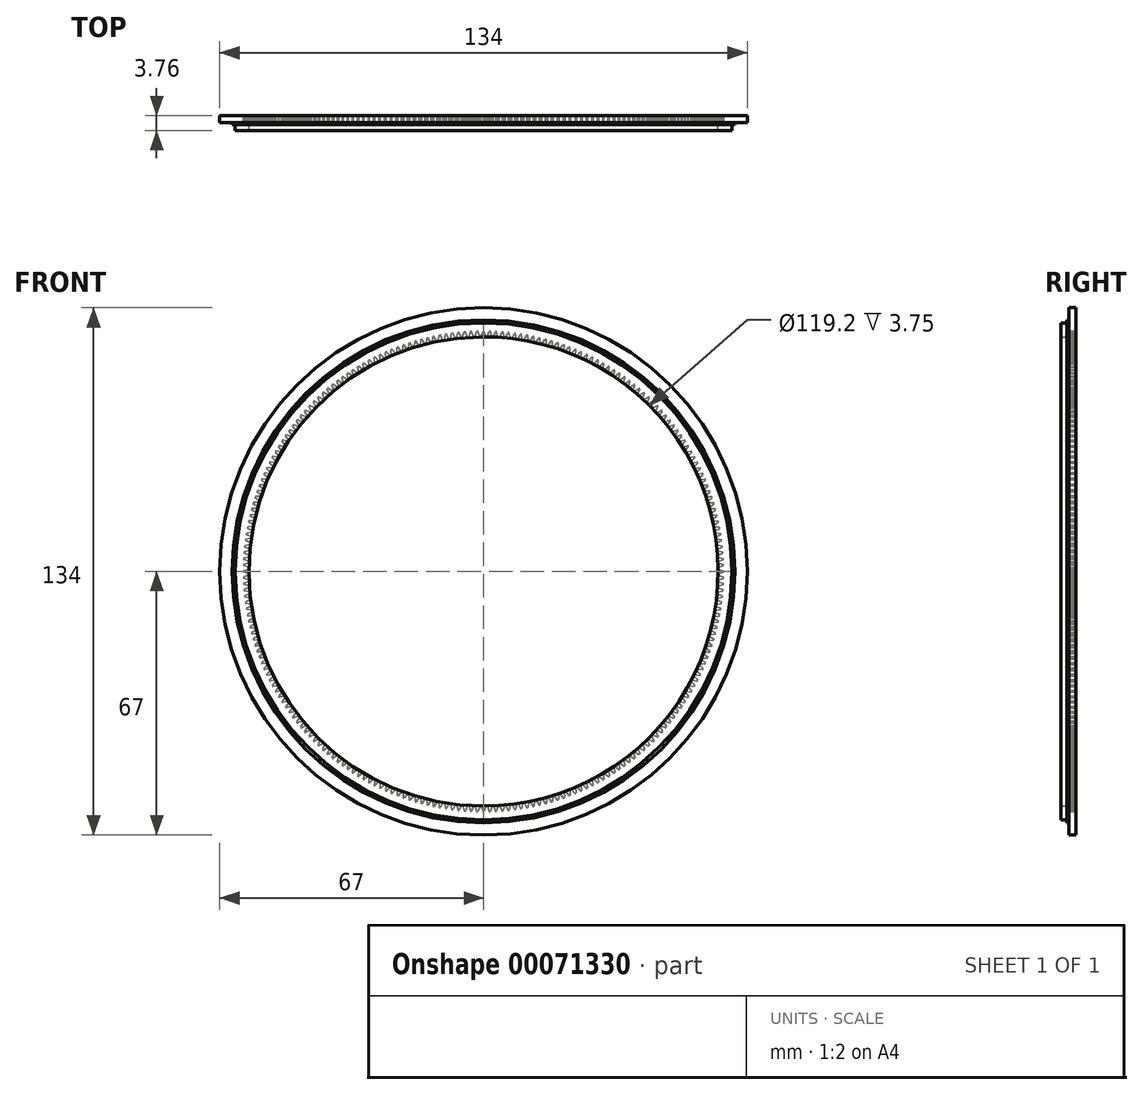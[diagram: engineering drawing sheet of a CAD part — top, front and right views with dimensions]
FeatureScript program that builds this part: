
annotation { "Feature Type Name" : "Feature", "Feature Type Description" : "" }
export const myFeature = defineFeature(function(context is Context, id is Id, definition is map)
    precondition{}
    {
        {
            var Q0;
            Q0=qCreatedBy(makeId("Front.planeOp"),FACE);
            var sketch = newSketch(context, id + "F0", { "sketchPlane" : qUnion([Q0])});
            skCircle(sketch, "E0", {"center": v(0, 0) * mm, "radius": 59.6 * mm});
            skCircle(sketch, "E1", {"center": v(0, 0) * mm, "radius": 67 * mm});
            skSolve(sketch);
        }
        {
            var Q0;
            Q0 = qSketchRegion(id + "F0", true);
            var Q1;
            Q1 = qSketchRegion(id + "F2", true);
            extrude(context, id + "F1", {"entities" : qUnion([Q0, Q1]), "endBound" : BoundingType.SYMMETRIC, "depth" : 3.75 * mm});
        }
        {
            var Q0;
            Q0=makeQuery(id+"F1.opExtrude","CAP_FACE",FACE,{"disambiguationData":[OSD([sQuery(id+"F0.wireOp",EDGE,"E0"),sQuery(id+"F0.wireOp",EDGE,"E1")])],"isStart":false});
            var sketch = newSketch(context, id + "F2", { "sketchPlane" : qUnion([Q0])});
            skCircle(sketch, "E2", {"center": v(0, 0) * mm, "radius": 63.12 * mm});
            skCircle(sketch, "E3", {"center": v(0, 0) * mm, "radius": 63.88 * mm});
            skSolve(sketch);
        }
        {
            var Q0;
            Q0 = qSketchRegion(id + "F2", true);
            extrude(context, id + "F3", {"entities" : qUnion([Q0]), "operationType" : NewBodyOperationType.REMOVE, "oppositeDirection" : true, "depth" : 1.5 * mm});
        }
        {
            var Q0;
            {var subQ0=sQuery(id+"F0.wireOp",EDGE,"E1");Q0=makeQuery(id+"F3.boolean.opBoolean","SPLIT",FACE,{"disambiguationData":[TD([makeQuery(id+"F1.opExtrude","SWEPT_FACE",FACE,{"disambiguationData":[OSD([subQ0])]})])],"derivedFrom":makeQuery(id+"F1.opExtrude","CAP_FACE",FACE,{"disambiguationData":[OSD([sQuery(id+"F0.wireOp",EDGE,"E0"),subQ0])],"isStart":false})});}
            extrude(context, id + "F4", {"entities" : qUnion([Q0]), "operationType" : NewBodyOperationType.REMOVE, "oppositeDirection" : true, "depth" : 2 * mm});
        }
        {
            var Q0;
            Q0=qCreatedBy(makeId("Front.planeOp"),FACE);
            var sketch = newSketch(context, id + "F5", { "sketchPlane" : qUnion([Q0])});
            skCircle(sketch, "E4", {"center": v(0, 0) * mm, "radius": 61 * mm});
            skLineSegment(sketch, "E5", {"start": v(0, 0) * mm, "end": v(-61, 0) * mm});
            skLineSegment(sketch, "E6", {"start": v(-61, 0.15) * mm, "end": v(-61, -0.15) * mm});
            skPoint(sketch, "E7", {"position": v(-59.4, 0) * mm});
            skLineSegment(sketch, "E8", {"start": v(-59.4, 0.67) * mm, "end": v(-59.4, -0.68) * mm});
            skLineSegment(sketch, "E9", {"start": v(-59.4, 0.68) * mm, "end": v(-61, 0.15) * mm});
            skLineSegment(sketch, "E10", {"start": v(-59.4, -0.68) * mm, "end": v(-61, -0.15) * mm});
            skSolve(sketch);
        }
        {
            var Q0;
            {var subQ3=sQuery(id+"F5.wireOp",EDGE,"E9");var subQ5=sQuery(id+"F5.wireOp",EDGE,"E8");var subQ7=makeQuery(id+"F5.imprint","INTERSECT",VERTEX,{"derivedFrom":[subQ5,subQ3]});Q0=makeQuery(id+"F5.imprint","IMPRINT",FACE,{"disambiguationData":[TD([[makeQuery(id+"F5.imprint","IMPRINT",EDGE,{"disambiguationData":[TD([[subQ7,-1.0]])],"derivedFrom":subQ5}),-1.0]])]});}
            var Q1;
            {var subQ3=sQuery(id+"F5.wireOp",EDGE,"E10");var subQ5=sQuery(id+"F5.wireOp",EDGE,"E8");var subQ7=makeQuery(id+"F5.imprint","INTERSECT",VERTEX,{"derivedFrom":[subQ5,subQ3]});Q1=makeQuery(id+"F5.imprint","IMPRINT",FACE,{"disambiguationData":[TD([[makeQuery(id+"F5.imprint","IMPRINT",EDGE,{"disambiguationData":[TD([[subQ7,1.0]])],"derivedFrom":subQ5}),-1.0]])]});}
            extrude(context, id + "F6", {"entities" : qUnion([Q0, Q1]), "operationType" : NewBodyOperationType.REMOVE, "oppositeDirection" : true, "depth" : 7.5 * mm});
        }
        {
            var Q0;
            Q0=makeQuery(id+"F6.boolean.opBoolean","COPY",FACE,{"derivedFrom":makeQuery(id+"F6.opExtrude","CAP_FACE",FACE,{"disambiguationData":[OSD([sQuery(id+"F5.wireOp",EDGE,"E4"),sQuery(id+"F5.wireOp",EDGE,"E8"),sQuery(id+"F5.wireOp",EDGE,"E9"),sQuery(id+"F5.wireOp",EDGE,"E10")])],"isStart":true})});
            var Q1;
            Q1=makeQuery(id+"F6.boolean.opBoolean","COPY",FACE,{"derivedFrom":makeQuery(id+"F6.opExtrude","SWEPT_FACE",FACE,{"disambiguationData":[OSD([sQuery(id+"F5.wireOp",EDGE,"E9")])]})});
            var Q2;
            Q2=makeQuery(id+"F6.boolean.opBoolean","COPY",FACE,{"derivedFrom":makeQuery(id+"F6.opExtrude","SWEPT_FACE",FACE,{"disambiguationData":[OSD([sQuery(id+"F5.wireOp",EDGE,"E10")])]})});
            var Q3;
            Q3=makeQuery(id+"F6.boolean.opBoolean","COPY",FACE,{"derivedFrom":makeQuery(id+"F6.opExtrude","SWEPT_FACE",FACE,{"disambiguationData":[OSD([sQuery(id+"F5.wireOp",EDGE,"E4")])]})});
            var Q4;
            Q4=sQuery(id+"F5.wireOp",EDGE,"E4");
            circularPattern(context, id + "F7", {"operationType" : NewBodyOperationType.REMOVE, "faces" : qUnion([Q0, Q1, Q2, Q3]), "axis" : qUnion([Q4]), "angle" : 360 * degree, "instanceCount" : 240, "equalSpace" : true, "patternType" : PatternType.FACE});
        }
    });
